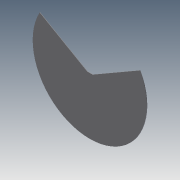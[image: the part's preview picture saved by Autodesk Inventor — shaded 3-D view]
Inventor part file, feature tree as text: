
AUTODESK INVENTOR PART (.ipt)
format: ipt  version: 2011 (Build 150239000, 239)  size: 78,336 bytes
history: native  units: in
note: dims shown in document units (in); Inventor stores cm internally (conversion verified against a paired STEP export)
features: extrude x2, sketch x2
ambient origin geometry x8: Origin, YZ Plane, XZ Plane, XY Plane, X Axis, Y Axis, Z Axis, Center Point
bodies: Solid1 (feature_tree)
feature tree (4):
  extrude  "Extrusion1"  Depth=0.0394in TaperAngle=0.0deg
  extrude  "Extrusion2"  Depth=0.5in
  sketch  "Sketch1"  dims[d0=10.0in d1=0.0394in d2=0.0in]
  sketch  "Sketch2"  dims[d3=0.25in d4=0.5in d5=150.0deg d6=30.0deg d7=0.0394in d8=0.0in]
